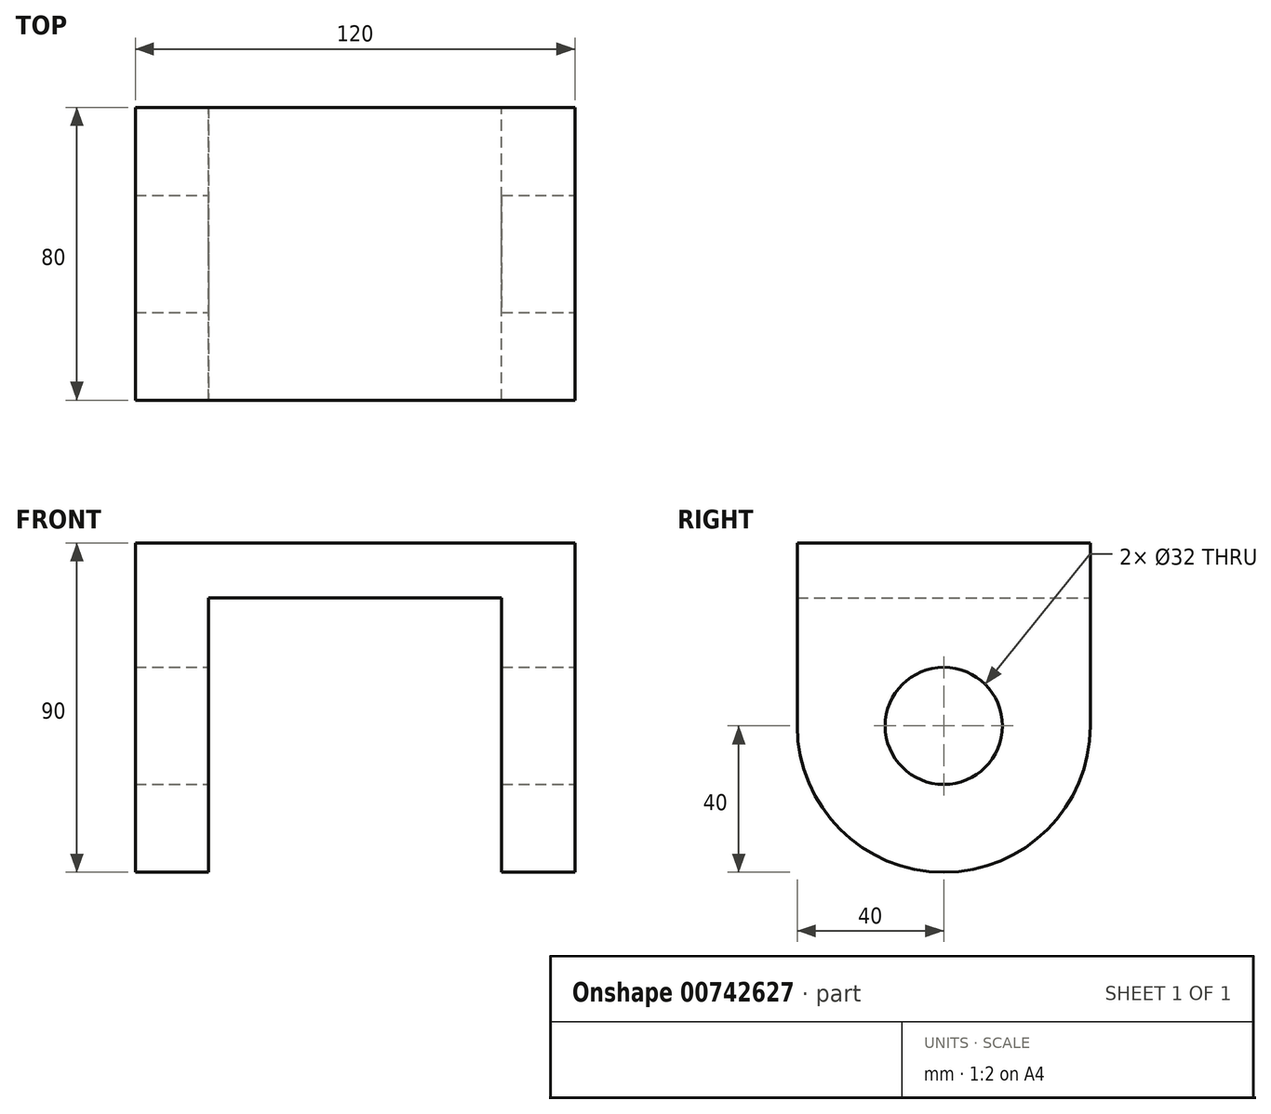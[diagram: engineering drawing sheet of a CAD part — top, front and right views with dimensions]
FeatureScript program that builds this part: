
annotation { "Feature Type Name" : "Feature", "Feature Type Description" : "" }
export const myFeature = defineFeature(function(context is Context, id is Id, definition is map)
    precondition{}
    {
        {
            var Q0;
            Q0=qCreatedBy(makeId("Front.planeOp"),FACE);
            var sketch = newSketch(context, id + "F0", { "sketchPlane" : qUnion([Q0])});
            skLineSegment(sketch, "E0.bottom", {"start": v(60, 45) * mm, "end": v(-60, 45) * mm});
            skLineSegment(sketch, "E0.top", {"start": v(60, -45) * mm, "end": v(-60, -45) * mm});
            skLineSegment(sketch, "E0.left", {"start": v(60, 45) * mm, "end": v(60, -45) * mm});
            skLineSegment(sketch, "E0.right", {"start": v(-60, 45) * mm, "end": v(-60, -45) * mm});
            skPoint(sketch, "E0.middle", {"position": v(0, 0) * mm});
            skLineSegment(sketch, "E1", {"start": v(-40, -45) * mm, "end": v(-40, 30) * mm});
            skLineSegment(sketch, "E2", {"start": v(-40, 30) * mm, "end": v(40, 30) * mm});
            skLineSegment(sketch, "E3", {"start": v(40, 30) * mm, "end": v(40, -45) * mm});
            skSolve(sketch);
        }
        {
            var Q0;
            Q0=makeQuery(id+"F0.imprint","IMPRINT",FACE,{"disambiguationData":[TD([[makeQuery(id+"F0.imprint","IMPRINT",EDGE,{"derivedFrom":sQuery(id+"F0.wireOp",EDGE,"E0.bottom")}),1.0]])]});
            extrude(context, id + "F1", {"entities" : qUnion([Q0]), "depth" : 80 * mm, "offsetDistance" : 25 * mm});
        }
        {
            var Q0;
            Q0=makeQuery(id+"F1.opExtrude","SWEPT_FACE",FACE,{"disambiguationData":[OSD([sQuery(id+"F0.wireOp",EDGE,"E0.left")])]});
            var sketch = newSketch(context, id + "F2", { "sketchPlane" : qUnion([Q0])});
            skCircle(sketch, "E4", {"center": v(-40, -5) * mm, "radius": 40 * mm});
            skCircle(sketch, "E5", {"center": v(-40, -5) * mm, "radius": 16 * mm});
            skSolve(sketch);
        }
        {
            var Q0;
            {var subQ0=sQuery(id+"F2.wireOp",EDGE,"E4");var subQ1=sQuery(id+"F0.wireOp",EDGE,"E0.left");var subQ2=makeQuery(id+"F1.opExtrude","CAP_EDGE",EDGE,{"disambiguationData":[OSD([subQ1])],"isStart":false});var subQ3=makeQuery(id+"F2.imprint","INTERSECT",VERTEX,{"derivedFrom":[subQ2,subQ0]});Q0=makeQuery(id+"F2.imprint","IMPRINT",FACE,{"disambiguationData":[TD([[makeQuery(id+"F2.imprint","IMPRINT",EDGE,{"disambiguationData":[TD([[subQ3,-1.0]])],"derivedFrom":subQ0}),-1.0]])]});}
            var Q1;
            {var subQ0=sQuery(id+"F2.wireOp",EDGE,"E4");var subQ1=sQuery(id+"F0.wireOp",EDGE,"E0.left");var subQ2=makeQuery(id+"F1.opExtrude","CAP_EDGE",EDGE,{"disambiguationData":[OSD([subQ1])],"isStart":true});var subQ3=makeQuery(id+"F2.imprint","INTERSECT",VERTEX,{"derivedFrom":[subQ2,subQ0]});Q1=makeQuery(id+"F2.imprint","IMPRINT",FACE,{"disambiguationData":[TD([[makeQuery(id+"F2.imprint","IMPRINT",EDGE,{"disambiguationData":[TD([[subQ3,1.0]])],"derivedFrom":subQ0}),-1.0]])]});}
            var Q2;
            Q2=makeQuery(id+"F2.imprint","IMPRINT",FACE,{"disambiguationData":[TD([[makeQuery(id+"F2.imprint","IMPRINT",EDGE,{"derivedFrom":sQuery(id+"F2.wireOp",EDGE,"E5")}),1.0]])]});
            extrude(context, id + "F3", {"entities" : qUnion([Q0, Q1, Q2]), "operationType" : NewBodyOperationType.REMOVE, "oppositeDirection" : true, "depth" : 120 * mm, "offsetDistance" : 25 * mm});
        }
        {
            var Q0;
            Q0=makeQuery(id+"F1.opExtrude","SWEPT_EDGE",EDGE,{"disambiguationData":[OSD([sQuery(id+"F0.wireOp",EDGE,"E0.bottom"),sQuery(id+"F0.wireOp",EDGE,"E0.right")])]});
            cPlane(context, id + "F4", {"entities" : qUnion([Q0]), "cplaneType" : CPlaneType.MID_PLANE, "offset" : 25 * mm, "width" : 150 * mm, "height" : 150 * mm});
        }
        {
            var Q0;
            Q0=qCreatedBy(id+"F4.planeOp",FACE);
            var sketch = newSketch(context, id + "F5", { "sketchPlane" : qUnion([Q0])});
            skLineSegment(sketch, "E6", {"start": v(27.69, 45) * mm, "end": v(27.69, 87) * mm});
            skLineSegment(sketch, "E7", {"start": v(27.69, 87) * mm, "end": v(15.98, 87) * mm});
            skLineSegment(sketch, "E8", {"start": v(15.98, 87) * mm, "end": v(15.98, 66.68) * mm});
            skLineSegment(sketch, "E9", {"start": v(15.98, 66.68) * mm, "end": v(5.23, 45) * mm});
            skLineSegment(sketch, "E10", {"start": v(5.23, 45) * mm, "end": v(27.69, 45) * mm});
            skLineSegment(sketch, "E11", {"start": v(0, 0) * mm, "end": v(0, 92.66) * mm, "construction": true});
            skSolve(sketch);
        }
        {
            var Q0;
            Q0 = qConstructionFilter(qBodyType(qCreatedBy(id + "F5" ,EDGE), BodyType.WIRE), ConstructionObject.NO);
            var Q1;
            Q1=sQuery(id+"F5.wireOp",EDGE,"E11");
            revolve(context, id + "F6", {"bodyType" : ToolBodyType.SURFACE, "surfaceOperationType" : NewSurfaceOperationType.NEW, "surfaceEntities" : qUnion([Q0]), "axis" : qUnion([Q1]), "revolveType" : RevolveType.FULL});
        }
    });
